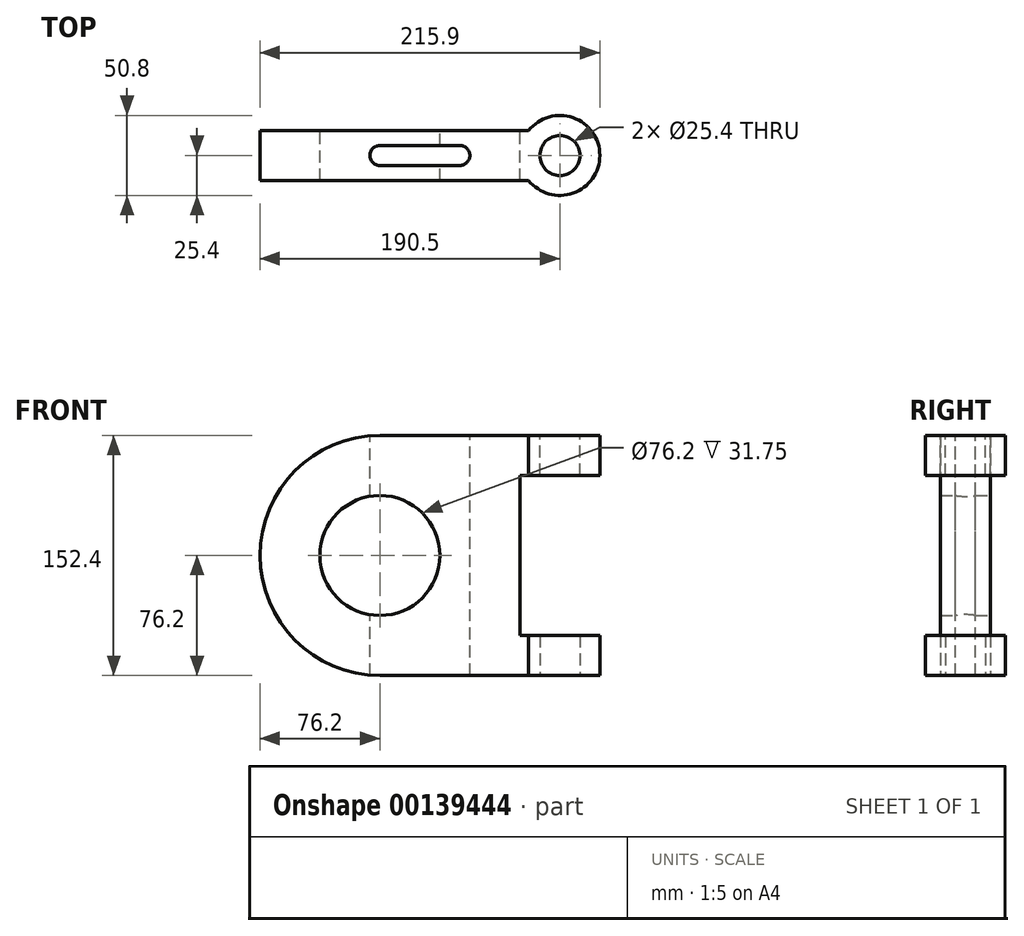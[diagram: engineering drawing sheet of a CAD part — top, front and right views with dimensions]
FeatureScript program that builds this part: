
annotation { "Feature Type Name" : "Feature", "Feature Type Description" : "" }
export const myFeature = defineFeature(function(context is Context, id is Id, definition is map)
    precondition{}
    {
        {
            var Q0;
            Q0=qCreatedBy(makeId("Front.planeOp"),FACE);
            var sketch = newSketch(context, id + "F0", { "sketchPlane" : qUnion([Q0])});
            skCircle(sketch, "E0", {"center": v(0, 0) * mm, "radius": 38.1 * mm});
            skArc(sketch, "E1", {"start": v(0, 76.2) * mm, "mid": v(-76.2, 0) * mm, "end": v(0, -76.2) * mm});
            skLineSegment(sketch, "E2", {"start": v(0, -76.2) * mm, "end": v(88.9, -76.2) * mm});
            skLineSegment(sketch, "E3", {"start": v(88.9, -76.2) * mm, "end": v(88.9, 76.2) * mm});
            skLineSegment(sketch, "E4", {"start": v(88.9, 76.2) * mm, "end": v(0, 76.2) * mm});
            skSolve(sketch);
        }
        {
            var Q0;
            Q0 = qSketchRegion(id + "F0", true);
            extrude(context, id + "F1", {"entities" : qUnion([Q0]), "endBound" : BoundingType.SYMMETRIC, "depth" : 31.75 * mm});
        }
        {
            var Q0;
            Q0=makeQuery(id+"F1.opExtrude","SWEPT_FACE",FACE,{"disambiguationData":[OSD([sQuery(id+"F0.wireOp",EDGE,"E4")])]});
            var sketch = newSketch(context, id + "F2", { "sketchPlane" : qUnion([Q0])});
            skArc(sketch, "E5", {"start": v(0, 6.35) * mm, "mid": v(-6.35, 0) * mm, "end": v(0, -6.35) * mm});
            skLineSegment(sketch, "E6", {"start": v(0, 6.35) * mm, "end": v(50.8, 6.35) * mm});
            skLineSegment(sketch, "E7", {"start": v(0, -6.35) * mm, "end": v(50.8, -6.35) * mm});
            skArc(sketch, "E8", {"start": v(50.8, -6.35) * mm, "mid": v(57.15, 0) * mm, "end": v(50.8, 6.35) * mm});
            skSolve(sketch);
        }
        {
            var Q0;
            Q0 = qSketchRegion(id + "F2", true);
            extrude(context, id + "F3", {"entities" : qUnion([Q0]), "operationType" : NewBodyOperationType.REMOVE, "endBound" : BoundingType.SYMMETRIC, "oppositeDirection" : true, "depth" : 477 * mm});
        }
        {
            var Q0;
            Q0=makeQuery(id+"F1.opExtrude","SWEPT_FACE",FACE,{"disambiguationData":[OSD([sQuery(id+"F0.wireOp",EDGE,"E4")])]});
            var sketch = newSketch(context, id + "F4", { "sketchPlane" : qUnion([Q0])});
            skPoint(sketch, "E9.centerSnap0", {"position": v(88.9, 0) * mm});
            skCircle(sketch, "E10", {"center": v(114.3, 0) * mm, "radius": 12.7 * mm});
            skCircle(sketch, "E11", {"center": v(114.3, 0) * mm, "radius": 25.4 * mm});
            skLineSegment(sketch, "E12", {"start": v(88.9, -15.88) * mm, "end": v(94.47, -15.88) * mm});
            skLineSegment(sketch, "E13", {"start": v(88.9, 15.88) * mm, "end": v(94.47, 15.88) * mm});
            skLineSegment(sketch, "E14.0", {"start": v(88.9, -15.88) * mm, "end": v(88.9, 15.88) * mm});
            skSolve(sketch);
        }
        {
            var Q0;
            {var subQ0=sQuery(id+"F4.wireOp",EDGE,"E12");Q0=makeQuery(id+"F4.imprint","IMPRINT",FACE,{"disambiguationData":[TD([[makeQuery(id+"F4.imprint","IMPRINT",EDGE,{"derivedFrom":subQ0}),1.0]])]});}
            var Q1;
            Q1=makeQuery(id+"F4.imprint","IMPRINT",FACE,{"disambiguationData":[TD([[makeQuery(id+"F4.imprint","IMPRINT",EDGE,{"derivedFrom":sQuery(id+"F4.wireOp",EDGE,"E10")}),-1.0]])]});
            var Q2;
            {var subQ0=sQuery(id+"F4.wireOp",EDGE,"E13");Q2=makeQuery(id+"F4.imprint","IMPRINT",FACE,{"disambiguationData":[TD([[makeQuery(id+"F4.imprint","IMPRINT",EDGE,{"derivedFrom":subQ0}),-1.0]])]});}
            extrude(context, id + "F5", {"entities" : qUnion([Q0, Q1, Q2]), "operationType" : NewBodyOperationType.ADD, "oppositeDirection" : true, "depth" : 25.4 * mm});
        }
        {
            var Q0;
            Q0=makeQuery(id+"F1.opExtrude","SWEPT_FACE",FACE,{"disambiguationData":[OSD([sQuery(id+"F0.wireOp",EDGE,"E2")])]});
            var sketch = newSketch(context, id + "F6", { "sketchPlane" : qUnion([Q0])});
            skPoint(sketch, "E15.centerSnap0", {"position": v(88.9, 0) * mm});
            skCircle(sketch, "E16", {"center": v(114.3, 0) * mm, "radius": 12.7 * mm});
            skCircle(sketch, "E17", {"center": v(114.3, 0) * mm, "radius": 25.4 * mm});
            skLineSegment(sketch, "E18", {"start": v(88.9, -15.87) * mm, "end": v(94.47, -15.87) * mm});
            skLineSegment(sketch, "E19", {"start": v(88.9, 15.88) * mm, "end": v(94.47, 15.88) * mm});
            skPoint(sketch, "E20", {"position": v(88.9, 15.88) * mm});
            skPoint(sketch, "E21", {"position": v(88.9, -15.88) * mm});
            skLineSegment(sketch, "E22", {"start": v(88.9, 15.88) * mm, "end": v(88.9, -15.87) * mm});
            skSolve(sketch);
        }
        {
            var Q0;
            Q0 = qSketchRegion(id + "F6", true);
            extrude(context, id + "F7", {"entities" : qUnion([Q0]), "operationType" : NewBodyOperationType.ADD, "oppositeDirection" : true, "depth" : 25.4 * mm});
        }
    });
